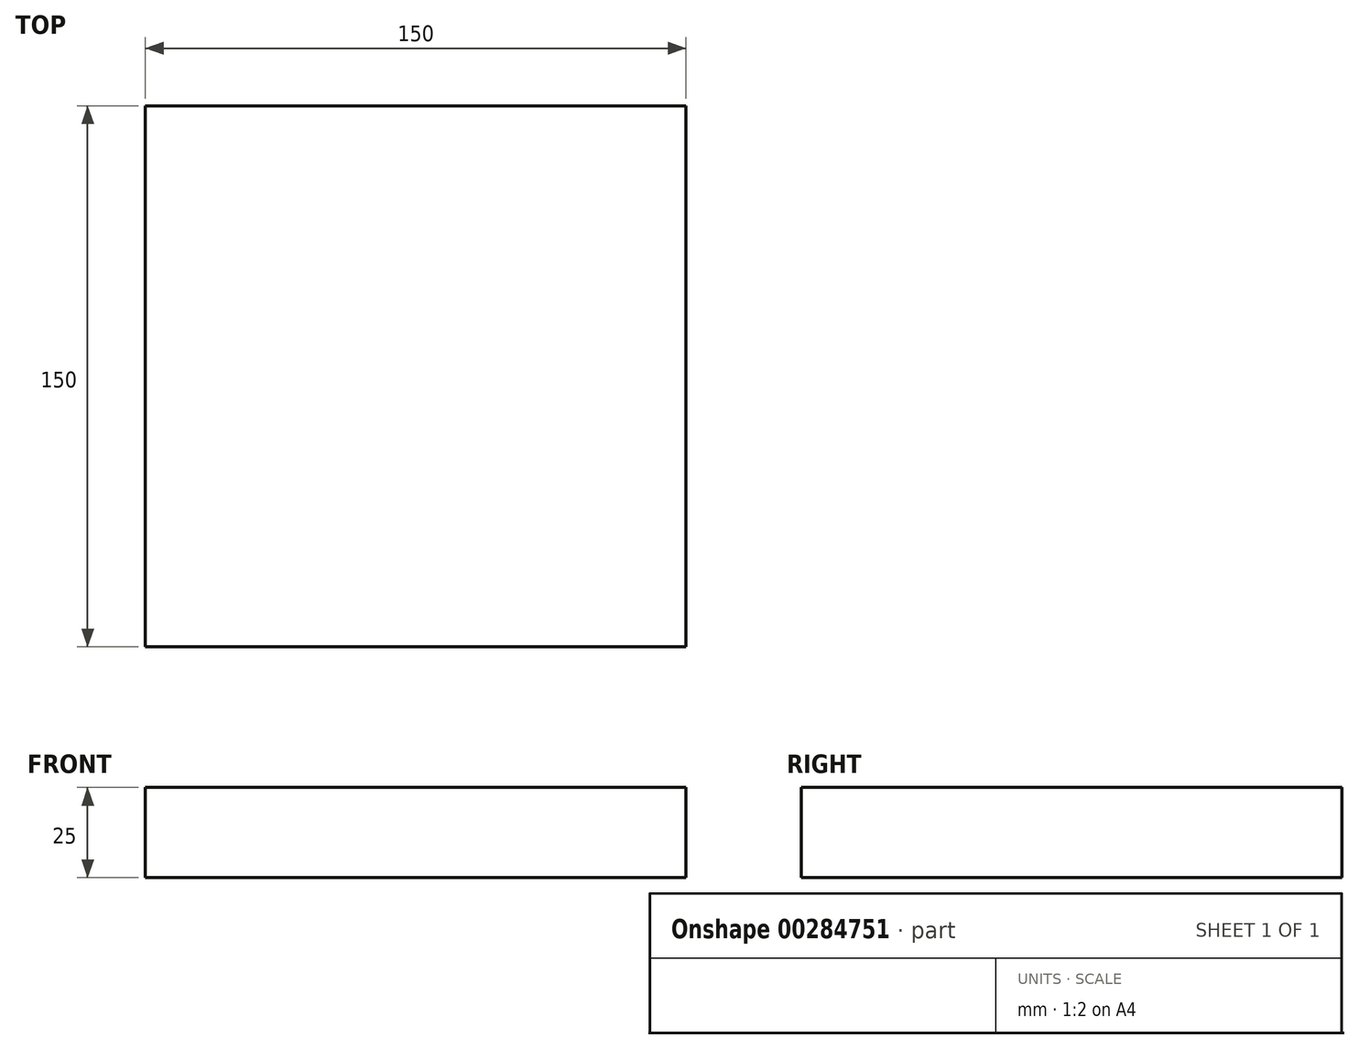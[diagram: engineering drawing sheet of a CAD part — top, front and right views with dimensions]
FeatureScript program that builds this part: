
annotation { "Feature Type Name" : "Feature", "Feature Type Description" : "" }
export const myFeature = defineFeature(function(context is Context, id is Id, definition is map)
    precondition{}
    {
        {
            var Q0;
            Q0=qCreatedBy(makeId("Top.planeOp"),FACE);
            var sketch = newSketch(context, id + "F0", { "sketchPlane" : qUnion([Q0])});
            skLineSegment(sketch, "E0.bottom", {"start": v(0, 0) * mm, "end": v(150, 0) * mm});
            skLineSegment(sketch, "E0.top", {"start": v(0, -150) * mm, "end": v(150, -150) * mm});
            skLineSegment(sketch, "E0.left", {"start": v(0, 0) * mm, "end": v(0, -150) * mm});
            skLineSegment(sketch, "E0.right", {"start": v(150, 0) * mm, "end": v(150, -150) * mm});
            skSolve(sketch);
        }
        {
            var Q0;
            Q0=makeQuery(id+"F0.imprint","IMPRINT",FACE,{"disambiguationData":[TD([[makeQuery(id+"F0.imprint","IMPRINT",EDGE,{"derivedFrom":sQuery(id+"F0.wireOp",EDGE,"E0.bottom")}),-1.0]])]});
            extrude(context, id + "F1", {"entities" : qUnion([Q0]), "depth" : 25 * mm});
        }
    });
